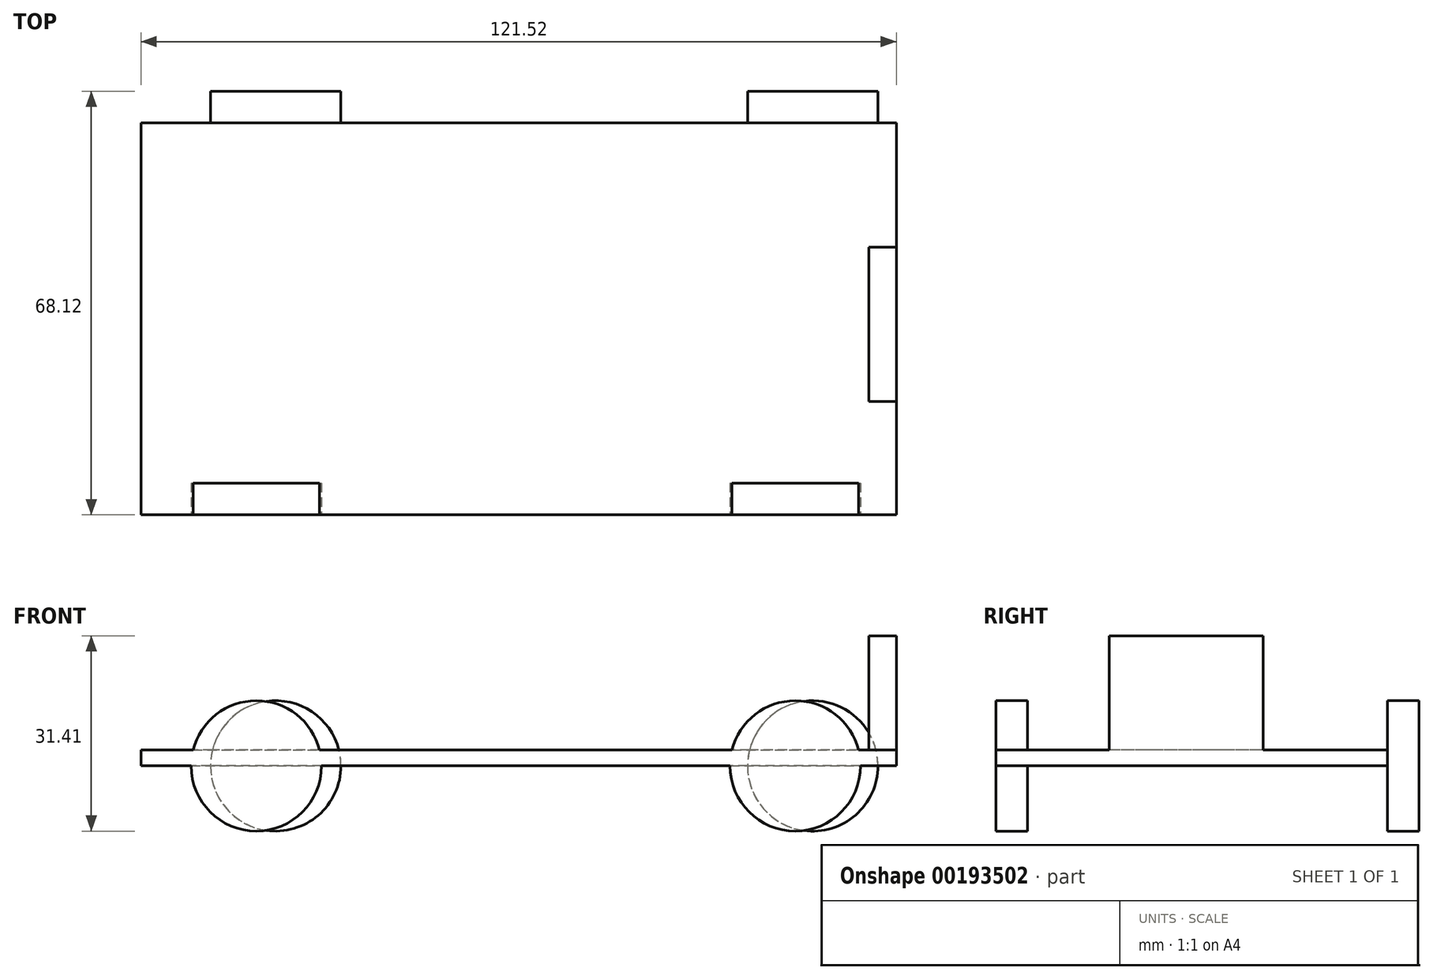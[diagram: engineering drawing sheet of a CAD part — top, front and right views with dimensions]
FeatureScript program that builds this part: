
annotation { "Feature Type Name" : "Feature", "Feature Type Description" : "" }
export const myFeature = defineFeature(function(context is Context, id is Id, definition is map)
    precondition{}
    {
        {
            var Q0;
            Q0=qCreatedBy(makeId("Top.planeOp"),FACE);
            var sketch = newSketch(context, id + "F0", { "sketchPlane" : qUnion([Q0])});
            skLineSegment(sketch, "E0.bottom", {"start": v(60.76, 31.52) * mm, "end": v(-60.76, 31.52) * mm});
            skLineSegment(sketch, "E0.top", {"start": v(60.76, -31.52) * mm, "end": v(-60.76, -31.52) * mm});
            skLineSegment(sketch, "E0.left", {"start": v(60.76, 31.52) * mm, "end": v(60.76, -31.52) * mm});
            skLineSegment(sketch, "E0.right", {"start": v(-60.76, 31.52) * mm, "end": v(-60.76, -31.52) * mm});
            skPoint(sketch, "E0.middle", {"position": v(0, 0) * mm});
            skSolve(sketch);
        }
        {
            var Q0;
            Q0=makeQuery(id+"F0.imprint","IMPRINT",FACE,{"disambiguationData":[TD([[makeQuery(id+"F0.imprint","IMPRINT",EDGE,{"derivedFrom":sQuery(id+"F0.wireOp",EDGE,"E0.bottom")}),1.0]])]});
            extrude(context, id + "F1", {"entities" : qUnion([Q0]), "depth" : 2.54 * mm});
        }
        {
            var Q0;
            Q0=makeQuery(id+"F1.opExtrude","SWEPT_FACE",FACE,{"disambiguationData":[OSD([sQuery(id+"F0.wireOp",EDGE,"E0.top")])]});
            var sketch = newSketch(context, id + "F2", { "sketchPlane" : qUnion([Q0])});
            skCircle(sketch, "E1", {"center": v(-42.22, 0) * mm, "radius": 10.5 * mm});
            skCircle(sketch, "E2", {"center": v(44.5, 0) * mm, "radius": 10.49 * mm});
            skSolve(sketch);
        }
        {
            var Q0;
            Q0=makeQuery(id+"F1.opExtrude","SWEPT_FACE",FACE,{"disambiguationData":[OSD([sQuery(id+"F0.wireOp",EDGE,"E0.bottom")])]});
            var sketch = newSketch(context, id + "F3", { "sketchPlane" : qUnion([Q0])});
            skCircle(sketch, "E3", {"center": v(-47.3, 0) * mm, "radius": 10.5 * mm});
            skCircle(sketch, "E4", {"center": v(39.1, 0) * mm, "radius": 10.5 * mm});
            skSolve(sketch);
        }
        {
            var Q0;
            Q0 = qSketchRegion(id + "F3", true);
            var Q1;
            Q1 = qSketchRegion(id + "F2", true);
            extrude(context, id + "F4", {"entities" : qUnion([Q0, Q1]), "operationType" : NewBodyOperationType.ADD, "depth" : 5.08 * mm});
        }
        {
            var Q0;
            Q0=makeQuery(id+"F1.opExtrude","SWEPT_FACE",FACE,{"disambiguationData":[OSD([sQuery(id+"F0.wireOp",EDGE,"E0.left")])]});
            var sketch = newSketch(context, id + "F5", { "sketchPlane" : qUnion([Q0])});
            skLineSegment(sketch, "E5.bottom", {"start": v(-13.28, 2.54) * mm, "end": v(11.51, 2.54) * mm});
            skLineSegment(sketch, "E5.top", {"start": v(-13.28, 20.92) * mm, "end": v(11.51, 20.92) * mm});
            skLineSegment(sketch, "E5.left", {"start": v(-13.28, 2.54) * mm, "end": v(-13.28, 20.92) * mm});
            skLineSegment(sketch, "E5.right", {"start": v(11.51, 2.54) * mm, "end": v(11.51, 20.92) * mm});
            skSolve(sketch);
        }
        {
            var Q0;
            Q0=makeQuery(id+"F5.imprint","IMPRINT",FACE,{"disambiguationData":[TD([[makeQuery(id+"F5.imprint","IMPRINT",EDGE,{"derivedFrom":sQuery(id+"F5.wireOp",EDGE,"E5.bottom")}),-1.0]])]});
            extrude(context, id + "F6", {"entities" : qUnion([Q0]), "operationType" : NewBodyOperationType.ADD, "oppositeDirection" : true, "depth" : 4.42 * mm});
        }
    });
